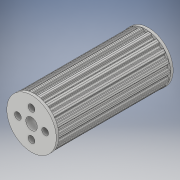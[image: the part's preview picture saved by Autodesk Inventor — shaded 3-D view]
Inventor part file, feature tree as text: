
AUTODESK INVENTOR PART (.ipt)
format: ipt  version: 2019 (Build 230136000, 136)  size: 855,040 bytes
history: native  units: in
note: dims shown in document units (in); Inventor stores cm internally (conversion verified against a paired STEP export)
features: sketch x6, extrude x5, other x2, pattern_circular x2, mirror x1, projected_geometry x1
ambient origin geometry x8: Origin, YZ Plane, XZ Plane, XY Plane, X Axis, Y Axis, Z Axis, Center Point
bodies: Solid1 (feature_tree)
feature tree (17):
  other  "Pulley"
  sketch  "Sketch1"  dims[d0=7.0866in d2=360.0deg d8=0.0049in d9=0.0in d10=7.0866in d11=360.0deg]
  extrude  "Extrusion1"  Depth=0.0049in TaperAngle=0.0deg
  pattern_circular  "Circular Pattern1"  Count=18 Angle=360.0deg
  extrude  "Extrusion2"  Depth=7.0866in TaperAngle=360.0deg
  pattern_circular  "Circular Pattern2"  [2 undecoded]
  extrude  "Extrusion3"  Depth=0.0625in
  extrude  "Extrusion4"  Depth=0.0625in
  mirror  "Mirror1"
  extrude  "Extrusion5"  Depth=0.0625in TaperAngle=360.0deg
  sketch  "Sketch2"  dims[d13=0.0049in d14=0.0in d15=7.0866in d16=360.0deg]
  sketch  "Sketch3"  dims[d18=1.3438in d19=0.0in]
  sketch  "Sketch4"  dims[d20=1.1417in]
  projected_geometry  "Projected Loop1"
  sketch  "Sketch5"  dims[d21=0.0625in d22=0.0in]
  sketch  "Sketch6"  dims[d23=0.0984in d24=0.2667in d25=0.1575in d26=0.315in d27=1.5748in d29=360.0deg d31=0.0625in d32=0.0in]
  other  "mmGroup0"
note: 2 required parameter values undecoded (feature->parameter linkage not recoverable at this tier; creation-order binding heuristic only, values carry confidence <= 0.55)
